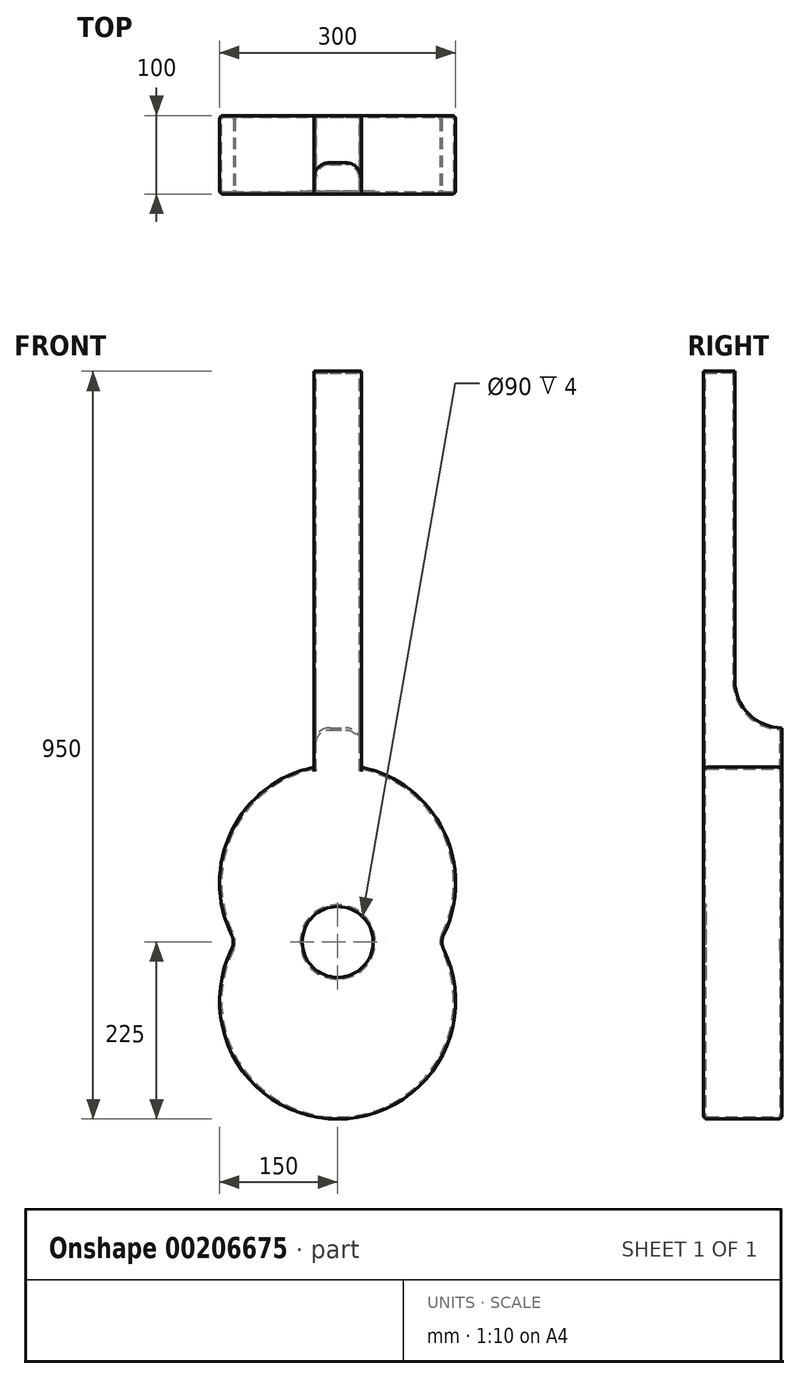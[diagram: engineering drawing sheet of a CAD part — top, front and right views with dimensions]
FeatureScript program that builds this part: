
annotation { "Feature Type Name" : "Feature", "Feature Type Description" : "" }
export const myFeature = defineFeature(function(context is Context, id is Id, definition is map)
    precondition{}
    {
        {
            var Q0;
            Q0=qCreatedBy(makeId("Front.planeOp"),FACE);
            var sketch = newSketch(context, id + "F0", { "sketchPlane" : qUnion([Q0])});
            skArc(sketch, "E0", {"start": v(-129.9, 225) * mm, "mid": v(0, 0) * mm, "end": v(129.9, 225) * mm});
            skArc(sketch, "E1", {"start": v(-30, 446.97) * mm, "mid": v(-136.78, 361.56) * mm, "end": v(-129.9, 225) * mm});
            skLineSegment(sketch, "E2.top", {"start": v(30, 950) * mm, "end": v(-30, 950) * mm});
            skLineSegment(sketch, "E2.left", {"start": v(30, 446.97) * mm, "end": v(30, 950) * mm});
            skLineSegment(sketch, "E2.right", {"start": v(-30, 446.97) * mm, "end": v(-30, 950) * mm});
            skPoint(sketch, "E2.middle", {"position": v(0, 625) * mm});
            skPoint(sketch, "E3.orphan", {"position": v(30, 300) * mm});
            skPoint(sketch, "E2.bottom.end.orphan", {"position": v(-30, 300) * mm});
            skArc(sketch, "E4.trimOffspring", {"start": v(129.9, 225) * mm, "mid": v(136.78, 361.56) * mm, "end": v(30, 446.97) * mm});
            skSolve(sketch);
        }
        {
            var Q0;
            Q0 = qSketchRegion(id + "F0", true);
            extrude(context, id + "F1", {"entities" : qUnion([Q0]), "depth" : 100 * mm});
        }
        {
            var Q0;
            Q0=qCreatedBy(makeId("Right.planeOp"),FACE);
            var sketch = newSketch(context, id + "F2", { "sketchPlane" : qUnion([Q0])});
            skLineSegment(sketch, "E5", {"start": v(-60, 950) * mm, "end": v(-60, 556.97) * mm});
            skArc(sketch, "E6", {"start": v(-60, 556.97) * mm, "mid": v(-42.43, 514.54) * mm, "end": v(0, 496.97) * mm});
            skLineSegment(sketch, "E7", {"start": v(-60, 950) * mm, "end": v(0, 950) * mm});
            skLineSegment(sketch, "E8", {"start": v(0, 950) * mm, "end": v(0, 496.97) * mm});
            skSolve(sketch);
        }
        {
            var Q0;
            Q0 = qSketchRegion(id + "F2", true);
            extrude(context, id + "F3", {"entities" : qUnion([Q0]), "operationType" : NewBodyOperationType.REMOVE, "endBound" : BoundingType.SYMMETRIC, "oppositeDirection" : true, "depth" : 100 * mm});
        }
        {
            var Q0;
            Q0=makeQuery(id+"F3.boolean.opBoolean","INTERSECT",EDGE,{"derivedFrom":[makeQuery(id+"F1.opExtrude","SWEPT_FACE",FACE,{"disambiguationData":[OSD([sQuery(id+"F0.wireOp",EDGE,"E2.left")])]}),makeQuery(id+"F3.opExtrude","SWEPT_FACE",FACE,{"disambiguationData":[OSD([sQuery(id+"F2.wireOp",EDGE,"E5")])]})]});
            var Q1;
            Q1=makeQuery(id+"F3.boolean.opBoolean","INTERSECT",EDGE,{"derivedFrom":[makeQuery(id+"F1.opExtrude","SWEPT_FACE",FACE,{"disambiguationData":[OSD([sQuery(id+"F0.wireOp",EDGE,"E2.right")])]}),makeQuery(id+"F3.opExtrude","SWEPT_FACE",FACE,{"disambiguationData":[OSD([sQuery(id+"F2.wireOp",EDGE,"E5")])]})]});
            var Q2;
            Q2=makeQuery(id+"F1.opExtrude","SWEPT_EDGE",EDGE,{"disambiguationData":[OSD([sQuery(id+"F0.wireOp",EDGE,"E0"),sQuery(id+"F0.wireOp",EDGE,"E4.trimOffspring")])]});
            var Q3;
            Q3=makeQuery(id+"F1.opExtrude","SWEPT_EDGE",EDGE,{"disambiguationData":[OSD([sQuery(id+"F0.wireOp",EDGE,"E0"),sQuery(id+"F0.wireOp",EDGE,"E1")])]});
            fillet(context, id + "F4", {"entities" : qUnion([Q0, Q1, Q2, Q3]), "radius" : 20 * mm, "tangentPropagation" : true, "allowEdgeOverflow" : false});
        }
        {
            var Q0;
            Q0=makeQuery(id+"F1.opExtrude","CAP_FACE",FACE,{"disambiguationData":[OSD([sQuery(id+"F0.wireOp",EDGE,"E0"),sQuery(id+"F0.wireOp",EDGE,"E1"),sQuery(id+"F0.wireOp",EDGE,"E2.top"),sQuery(id+"F0.wireOp",EDGE,"E2.left"),sQuery(id+"F0.wireOp",EDGE,"E2.right"),sQuery(id+"F0.wireOp",EDGE,"E4.trimOffspring")])],"isStart":false});
            var sketch = newSketch(context, id + "F5", { "sketchPlane" : qUnion([Q0])});
            skLineSegment(sketch, "E9", {"start": v(-129.9, 225) * mm, "end": v(129.9, 225) * mm, "construction": true});
            skCircle(sketch, "E10", {"center": v(0, 225) * mm, "radius": 45 * mm});
            skSolve(sketch);
        }
        {
            var Q0;
            Q0 = qSketchRegion(id + "F5", true);
            extrude(context, id + "F6", {"entities" : qUnion([Q0]), "operationType" : NewBodyOperationType.REMOVE, "oppositeDirection" : true, "depth" : 4 * mm});
        }
        {
            var Q0;
            Q0=makeQuery(id+"F1.opExtrude","CAP_EDGE",EDGE,{"disambiguationData":[OSD([sQuery(id+"F0.wireOp",EDGE,"E1")])],"isStart":false});
            var Q1;
            Q1=makeQuery(id+"F1.opExtrude","CAP_EDGE",EDGE,{"disambiguationData":[OSD([sQuery(id+"F0.wireOp",EDGE,"E1")])],"isStart":true});
            fillet(context, id + "F7", {"entities" : qUnion([Q0, Q1]), "radius" : 5 * mm, "tangentPropagation" : true, "allowEdgeOverflow" : false});
        }
        {
            var Q0;
            Q0=makeQuery(id+"F6.boolean.opBoolean","COPY",FACE,{"derivedFrom":makeQuery(id+"F6.opExtrude","CAP_FACE",FACE,{"disambiguationData":[OSD([sQuery(id+"F5.wireOp",EDGE,"E10")])],"isStart":false})});
            shell(context, id + "F8", {"entities" : qUnion([Q0]), "thickness" : 2.5 * mm});
        }
    });
